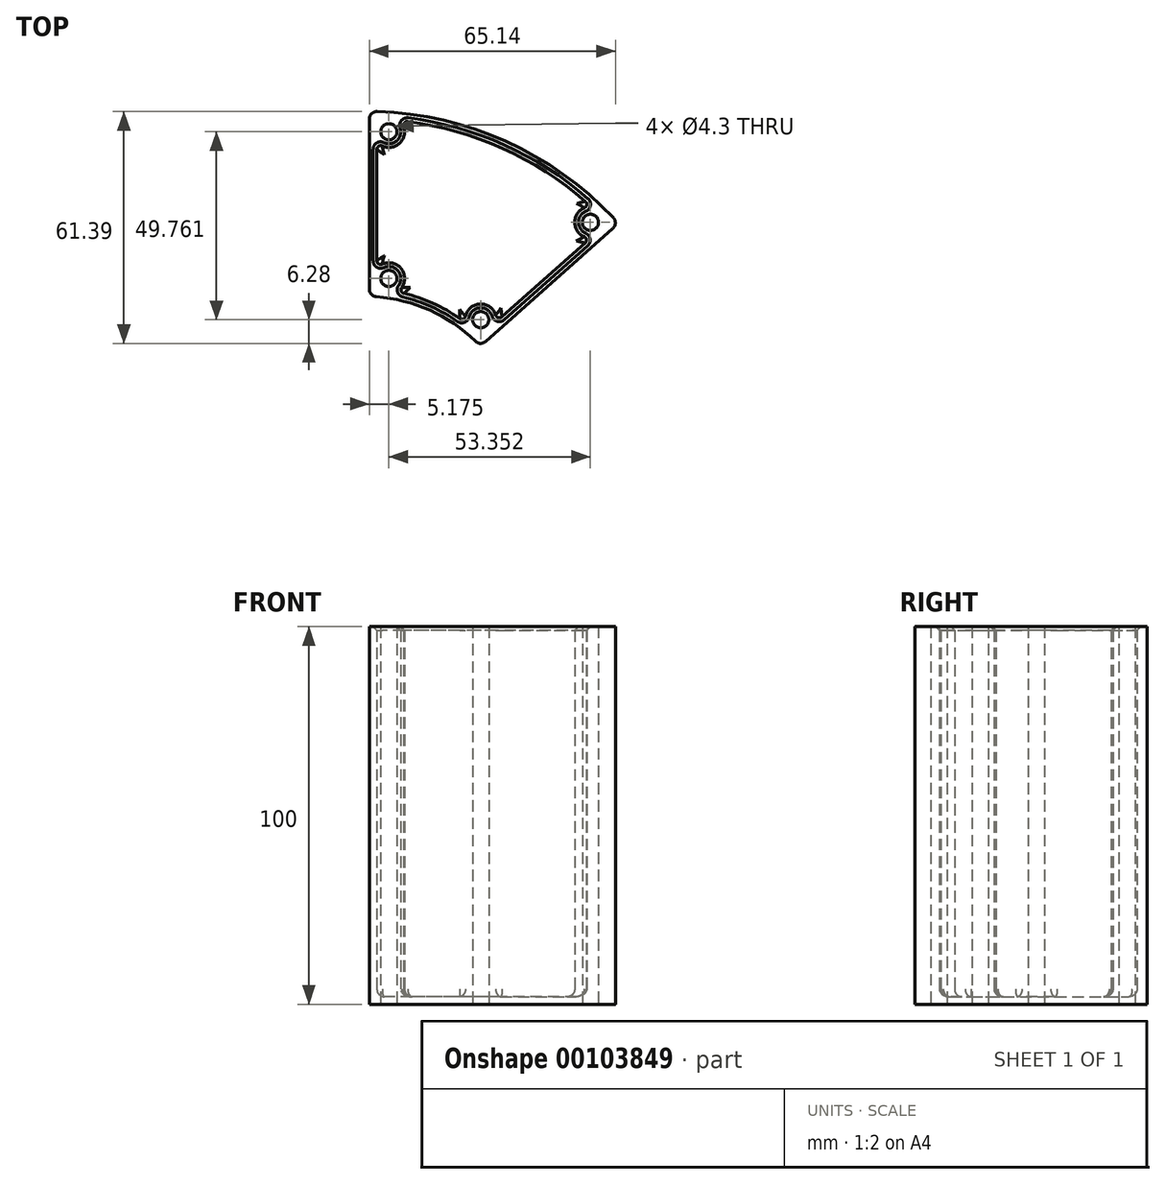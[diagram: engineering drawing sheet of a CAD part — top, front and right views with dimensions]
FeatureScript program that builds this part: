
annotation { "Feature Type Name" : "Feature", "Feature Type Description" : "" }
export const myFeature = defineFeature(function(context is Context, id is Id, definition is map)
    precondition{}
    {
        {
            var Q0;
            Q0=qCreatedBy(makeId("Top.planeOp"),FACE);
            var sketch = newSketch(context, id + "F0", { "sketchPlane" : qUnion([Q0])});
            skArc(sketch, "E0", {"start": v(30.28, 26.9) * mm, "mid": v(16.6, 36.94) * mm, "end": v(0, 40.5) * mm});
            skLineSegment(sketch, "E1", {"start": v(0, 40.5) * mm, "end": v(0, 91.5) * mm});
            skLineSegment(sketch, "E2", {"start": v(30.28, 26.9) * mm, "end": v(68.41, 60.76) * mm});
            skArc(sketch, "E3", {"start": v(0, 91.5) * mm, "mid": v(-37.5, -83.46) * mm, "end": v(68.41, 60.76) * mm});
            skArc(sketch, "E4", {"start": v(68.41, 60.76) * mm, "mid": v(37.5, 83.46) * mm, "end": v(0, 91.5) * mm});
            skLineSegment(sketch, "E5.0", {"start": v(1, 43.4) * mm, "end": v(1, 88.45) * mm});
            skArc(sketch, "E5.1", {"start": v(29.05, 29.63) * mm, "mid": v(17, 37.85) * mm, "end": v(2.86, 41.4) * mm});
            skLineSegment(sketch, "E5.2", {"start": v(31.78, 29.57) * mm, "end": v(65.47, 59.48) * mm});
            skArc(sketch, "E5.3", {"start": v(65.59, 62.36) * mm, "mid": v(37.1, 82.55) * mm, "end": v(3.07, 90.45) * mm});
            skCircle(sketch, "E6", {"center": v(6.17, 85.1) * mm, "radius": 2.15 * mm});
            skCircle(sketch, "E7", {"center": v(59.53, 61.13) * mm, "radius": 2.15 * mm});
            skCircle(sketch, "E8", {"center": v(30.5, 35.34) * mm, "radius": 2.15 * mm});
            skCircle(sketch, "E9", {"center": v(6.17, 46.26) * mm, "radius": 2.15 * mm});
            skLineSegment(sketch, "E10.0", {"start": v(3, 50.93) * mm, "end": v(3, 80.43) * mm});
            skArc(sketch, "E10.1", {"start": v(24.9, 35.67) * mm, "mid": v(17.83, 39.68) * mm, "end": v(10.14, 42.3) * mm});
            skLineSegment(sketch, "E10.2", {"start": v(36.09, 36.07) * mm, "end": v(58.15, 55.66) * mm});
            skArc(sketch, "E10.3", {"start": v(58.23, 66.65) * mm, "mid": v(36.27, 80.73) * mm, "end": v(11.16, 87.8) * mm});
            skArc(sketch, "E11", {"start": v(4.42, 81.34) * mm, "mid": v(8.96, 82.02) * mm, "end": v(10.1, 86.47) * mm});
            skArc(sketch, "E12", {"start": v(57.95, 64.97) * mm, "mid": v(55.38, 61.17) * mm, "end": v(57.88, 57.32) * mm});
            skArc(sketch, "E13", {"start": v(34.47, 36.53) * mm, "mid": v(30.36, 39.49) * mm, "end": v(26.45, 36.27) * mm});
            skArc(sketch, "E14", {"start": v(9.55, 43.86) * mm, "mid": v(9.37, 48.92) * mm, "end": v(4.42, 50.03) * mm});
            skPoint(sketch, "E15.visualSharp", {"position": v(9.12, 88.03) * mm});
            skArc(sketch, "E15.filletArc", {"start": v(11.16, 87.8) * mm, "mid": v(10.26, 87.43) * mm, "end": v(10.1, 86.47) * mm});
            skPoint(sketch, "E16.visualSharp", {"position": v(3, 82.43) * mm});
            skArc(sketch, "E16.filletArc", {"start": v(4.42, 81.34) * mm, "mid": v(3.46, 81.28) * mm, "end": v(3, 80.43) * mm});
            skPoint(sketch, "E17.visualSharp", {"position": v(3, 48.94) * mm});
            skArc(sketch, "E17.filletArc", {"start": v(3, 50.93) * mm, "mid": v(3.46, 50.09) * mm, "end": v(4.42, 50.03) * mm});
            skPoint(sketch, "E18.visualSharp", {"position": v(8.3, 42.7) * mm});
            skArc(sketch, "E18.filletArc", {"start": v(9.55, 43.86) * mm, "mid": v(9.43, 42.92) * mm, "end": v(10.14, 42.3) * mm});
            skPoint(sketch, "E19.visualSharp", {"position": v(26.41, 34.56) * mm});
            skArc(sketch, "E19.filletArc", {"start": v(24.9, 35.67) * mm, "mid": v(25.83, 35.56) * mm, "end": v(26.45, 36.27) * mm});
            skPoint(sketch, "E20.visualSharp", {"position": v(34.6, 34.74) * mm});
            skArc(sketch, "E20.filletArc", {"start": v(34.47, 36.53) * mm, "mid": v(35.15, 35.85) * mm, "end": v(36.09, 36.07) * mm});
            skPoint(sketch, "E21.visualSharp", {"position": v(59.64, 56.98) * mm});
            skArc(sketch, "E21.filletArc", {"start": v(58.15, 55.66) * mm, "mid": v(58.47, 56.56) * mm, "end": v(57.88, 57.32) * mm});
            skPoint(sketch, "E22.visualSharp", {"position": v(59.76, 65.27) * mm});
            skArc(sketch, "E22.filletArc", {"start": v(57.95, 64.97) * mm, "mid": v(58.56, 65.73) * mm, "end": v(58.23, 66.65) * mm});
            skPoint(sketch, "E23.visualSharp", {"position": v(1, 90.5) * mm});
            skArc(sketch, "E23.filletArc", {"start": v(3.07, 90.45) * mm, "mid": v(1.6, 89.89) * mm, "end": v(1, 88.45) * mm});
            skPoint(sketch, "E24.visualSharp", {"position": v(1, 41.49) * mm});
            skArc(sketch, "E24.filletArc", {"start": v(1, 43.4) * mm, "mid": v(1.54, 42.03) * mm, "end": v(2.86, 41.4) * mm});
            skPoint(sketch, "E25.visualSharp", {"position": v(30.36, 28.3) * mm});
            skArc(sketch, "E25.filletArc", {"start": v(29.05, 29.63) * mm, "mid": v(30.4, 29.06) * mm, "end": v(31.78, 29.57) * mm});
            skPoint(sketch, "E26.visualSharp", {"position": v(67, 60.84) * mm});
            skArc(sketch, "E26.filletArc", {"start": v(65.47, 59.48) * mm, "mid": v(66.14, 60.9) * mm, "end": v(65.59, 62.36) * mm});
            skSolve(sketch);
        }
        {
            var Q0;
            Q0=makeQuery(id+"F0.imprint","IMPRINT",FACE,{"disambiguationData":[TD([[makeQuery(id+"F0.imprint","IMPRINT",EDGE,{"derivedFrom":sQuery(id+"F0.wireOp",EDGE,"E5.0")}),-1.0]])]});
            var Q1;
            {var subQ1=sQuery(id+"F0.wireOp",EDGE,"b1673f46-570e-4e34-a5b0-88a3ac622ac5.0");Q1=makeQuery(id+"F0.imprint","IMPRINT",FACE,{"disambiguationData":[TD([[makeQuery(id+"F0.imprint","IMPRINT",EDGE,{"derivedFrom":subQ1}),1.0]])]});}
            var Q2;
            {var subQ1=sQuery(id+"F0.wireOp",EDGE,"b1673f46-570e-4e34-a5b0-88a3ac622ac5.0");Q2=makeQuery(id+"F0.imprint","IMPRINT",FACE,{"disambiguationData":[TD([[makeQuery(id+"F0.imprint","IMPRINT",EDGE,{"derivedFrom":subQ1}),-1.0]])]});}
            var Q3;
            Q3=makeQuery(id+"F0.imprint","IMPRINT",FACE,{"disambiguationData":[TD([[makeQuery(id+"F0.imprint","IMPRINT",EDGE,{"derivedFrom":sQuery(id+"F0.wireOp",EDGE,"E10.3")}),1.0]])]});
            var Q4;
            {var subQ1=sQuery(id+"F0.wireOp",EDGE,"b1673f46-570e-4e34-a5b0-88a3ac622ac5.2");Q4=makeQuery(id+"F0.imprint","IMPRINT",FACE,{"disambiguationData":[TD([[makeQuery(id+"F0.imprint","IMPRINT",EDGE,{"derivedFrom":subQ1}),-1.0]])]});}
            var Q5;
            {var subQ1=sQuery(id+"F0.wireOp",EDGE,"b1673f46-570e-4e34-a5b0-88a3ac622ac5.1");Q5=makeQuery(id+"F0.imprint","IMPRINT",FACE,{"disambiguationData":[TD([[makeQuery(id+"F0.imprint","IMPRINT",EDGE,{"derivedFrom":subQ1}),1.0]])]});}
            extrude(context, id + "F1", {"entities" : qUnion([Q0, Q1, Q2, Q3, Q4, Q5]), "depth" : 2 * mm});
        }
        {
            var Q0;
            Q0=makeQuery(id+"F0.imprint","IMPRINT",FACE,{"disambiguationData":[TD([[makeQuery(id+"F0.imprint","IMPRINT",EDGE,{"derivedFrom":sQuery(id+"F0.wireOp",EDGE,"E5.0")}),-1.0]])]});
            extrude(context, id + "F2", {"entities" : qUnion([Q0]), "depth" : 100 * mm});
        }
        {
            var Q0;
            Q0=makeQuery(id+"F2.opExtrude","SWEPT_BODY",BODY,{"disambiguationData":[OSD([sQuery(id+"F0.wireOp",EDGE,"E5.0"),sQuery(id+"F0.wireOp",EDGE,"E5.1"),sQuery(id+"F0.wireOp",EDGE,"E5.2"),sQuery(id+"F0.wireOp",EDGE,"E5.3"),sQuery(id+"F0.wireOp",EDGE,"E6"),sQuery(id+"F0.wireOp",EDGE,"E7"),sQuery(id+"F0.wireOp",EDGE,"E8"),sQuery(id+"F0.wireOp",EDGE,"E9"),sQuery(id+"F0.wireOp",EDGE,"E10.0"),sQuery(id+"F0.wireOp",EDGE,"E10.1"),sQuery(id+"F0.wireOp",EDGE,"E10.2"),sQuery(id+"F0.wireOp",EDGE,"E10.3"),sQuery(id+"F0.wireOp",EDGE,"E11"),sQuery(id+"F0.wireOp",EDGE,"E12"),sQuery(id+"F0.wireOp",EDGE,"E13"),sQuery(id+"F0.wireOp",EDGE,"E14"),sQuery(id+"F0.wireOp",EDGE,"E15.filletArc"),sQuery(id+"F0.wireOp",EDGE,"E16.filletArc"),sQuery(id+"F0.wireOp",EDGE,"E17.filletArc"),sQuery(id+"F0.wireOp",EDGE,"E18.filletArc"),sQuery(id+"F0.wireOp",EDGE,"E19.filletArc"),sQuery(id+"F0.wireOp",EDGE,"E20.filletArc"),sQuery(id+"F0.wireOp",EDGE,"E21.filletArc"),sQuery(id+"F0.wireOp",EDGE,"E22.filletArc"),sQuery(id+"F0.wireOp",EDGE,"E23.filletArc"),sQuery(id+"F0.wireOp",EDGE,"E24.filletArc"),sQuery(id+"F0.wireOp",EDGE,"E25.filletArc"),sQuery(id+"F0.wireOp",EDGE,"E26.filletArc")])]});
            var Q1;
            Q1=makeQuery(id+"F1.opExtrude","SWEPT_BODY",BODY,{"disambiguationData":[OSD([sQuery(id+"F0.wireOp",EDGE,"E5.0"),sQuery(id+"F0.wireOp",EDGE,"E5.1"),sQuery(id+"F0.wireOp",EDGE,"E5.2"),sQuery(id+"F0.wireOp",EDGE,"E5.3"),sQuery(id+"F0.wireOp",EDGE,"E6"),sQuery(id+"F0.wireOp",EDGE,"E7"),sQuery(id+"F0.wireOp",EDGE,"E8"),sQuery(id+"F0.wireOp",EDGE,"E9"),sQuery(id+"F0.wireOp",EDGE,"E23.filletArc"),sQuery(id+"F0.wireOp",EDGE,"E24.filletArc"),sQuery(id+"F0.wireOp",EDGE,"E25.filletArc"),sQuery(id+"F0.wireOp",EDGE,"E26.filletArc")])]});
            booleanBodies(context, id + "F3", {"operationType" : BooleanOperationType.UNION, "tools" : qUnion([Q0, Q1])});
        }
        {
            var Q0;
            Q0=makeQuery(id+"F3.opBoolean","INTERSECT",EDGE,{"derivedFrom":[makeQuery(id+"F1.opExtrude","CAP_FACE",FACE,{"disambiguationData":[OSD([sQuery(id+"F0.wireOp",EDGE,"E5.0"),sQuery(id+"F0.wireOp",EDGE,"E5.1"),sQuery(id+"F0.wireOp",EDGE,"E5.2"),sQuery(id+"F0.wireOp",EDGE,"E5.3"),sQuery(id+"F0.wireOp",EDGE,"E6"),sQuery(id+"F0.wireOp",EDGE,"E7"),sQuery(id+"F0.wireOp",EDGE,"E8"),sQuery(id+"F0.wireOp",EDGE,"E9"),sQuery(id+"F0.wireOp",EDGE,"E23.filletArc"),sQuery(id+"F0.wireOp",EDGE,"E24.filletArc"),sQuery(id+"F0.wireOp",EDGE,"E25.filletArc"),sQuery(id+"F0.wireOp",EDGE,"E26.filletArc")])],"isStart":false}),makeQuery(id+"F2.opExtrude","SWEPT_FACE",FACE,{"disambiguationData":[OSD([sQuery(id+"F0.wireOp",EDGE,"E10.0")])]})]});
            var Q1;
            Q1=makeQuery(id+"F3.opBoolean","INTERSECT",EDGE,{"derivedFrom":[makeQuery(id+"F1.opExtrude","CAP_FACE",FACE,{"disambiguationData":[OSD([sQuery(id+"F0.wireOp",EDGE,"E5.0"),sQuery(id+"F0.wireOp",EDGE,"E5.1"),sQuery(id+"F0.wireOp",EDGE,"E5.2"),sQuery(id+"F0.wireOp",EDGE,"E5.3"),sQuery(id+"F0.wireOp",EDGE,"E6"),sQuery(id+"F0.wireOp",EDGE,"E7"),sQuery(id+"F0.wireOp",EDGE,"E8"),sQuery(id+"F0.wireOp",EDGE,"E9"),sQuery(id+"F0.wireOp",EDGE,"E23.filletArc"),sQuery(id+"F0.wireOp",EDGE,"E24.filletArc"),sQuery(id+"F0.wireOp",EDGE,"E25.filletArc"),sQuery(id+"F0.wireOp",EDGE,"E26.filletArc")])],"isStart":false}),makeQuery(id+"F2.opExtrude","SWEPT_FACE",FACE,{"disambiguationData":[OSD([sQuery(id+"F0.wireOp",EDGE,"E16.filletArc")])]})]});
            fillet(context, id + "F4", {"entities" : qUnion([Q0, Q1]), "radius" : 2 * mm, "tangentPropagation" : true, "allowEdgeOverflow" : false});
        }
        {
            var Q0;
            Q0=makeQuery(id+"F2.opExtrude","CAP_EDGE",EDGE,{"disambiguationData":[OSD([sQuery(id+"F0.wireOp",EDGE,"E10.0")])],"isStart":false});
            var Q1;
            Q1=makeQuery(id+"F2.opExtrude","CAP_EDGE",EDGE,{"disambiguationData":[OSD([sQuery(id+"F0.wireOp",EDGE,"E17.filletArc")])],"isStart":false});
            var Q2;
            Q2=makeQuery(id+"F2.opExtrude","CAP_EDGE",EDGE,{"disambiguationData":[OSD([sQuery(id+"F0.wireOp",EDGE,"E14")])],"isStart":false});
            var Q3;
            Q3=makeQuery(id+"F2.opExtrude","CAP_EDGE",EDGE,{"disambiguationData":[OSD([sQuery(id+"F0.wireOp",EDGE,"E18.filletArc")])],"isStart":false});
            var Q4;
            Q4=makeQuery(id+"F2.opExtrude","CAP_EDGE",EDGE,{"disambiguationData":[OSD([sQuery(id+"F0.wireOp",EDGE,"E10.1")])],"isStart":false});
            var Q5;
            Q5=makeQuery(id+"F2.opExtrude","CAP_EDGE",EDGE,{"disambiguationData":[OSD([sQuery(id+"F0.wireOp",EDGE,"E19.filletArc")])],"isStart":false});
            var Q6;
            Q6=makeQuery(id+"F2.opExtrude","CAP_EDGE",EDGE,{"disambiguationData":[OSD([sQuery(id+"F0.wireOp",EDGE,"E13")])],"isStart":false});
            var Q7;
            Q7=makeQuery(id+"F2.opExtrude","CAP_EDGE",EDGE,{"disambiguationData":[OSD([sQuery(id+"F0.wireOp",EDGE,"E20.filletArc")])],"isStart":false});
            var Q8;
            Q8=makeQuery(id+"F2.opExtrude","CAP_EDGE",EDGE,{"disambiguationData":[OSD([sQuery(id+"F0.wireOp",EDGE,"E10.2")])],"isStart":false});
            var Q9;
            Q9=makeQuery(id+"F2.opExtrude","CAP_EDGE",EDGE,{"disambiguationData":[OSD([sQuery(id+"F0.wireOp",EDGE,"E21.filletArc")])],"isStart":false});
            var Q10;
            Q10=makeQuery(id+"F2.opExtrude","CAP_EDGE",EDGE,{"disambiguationData":[OSD([sQuery(id+"F0.wireOp",EDGE,"E12")])],"isStart":false});
            var Q11;
            Q11=makeQuery(id+"F2.opExtrude","CAP_EDGE",EDGE,{"disambiguationData":[OSD([sQuery(id+"F0.wireOp",EDGE,"E22.filletArc")])],"isStart":false});
            var Q12;
            Q12=makeQuery(id+"F2.opExtrude","CAP_EDGE",EDGE,{"disambiguationData":[OSD([sQuery(id+"F0.wireOp",EDGE,"E10.3")])],"isStart":false});
            var Q13;
            Q13=makeQuery(id+"F2.opExtrude","CAP_EDGE",EDGE,{"disambiguationData":[OSD([sQuery(id+"F0.wireOp",EDGE,"E11")])],"isStart":false});
            var Q14;
            Q14=makeQuery(id+"F2.opExtrude","CAP_EDGE",EDGE,{"disambiguationData":[OSD([sQuery(id+"F0.wireOp",EDGE,"E15.filletArc")])],"isStart":false});
            var Q15;
            Q15=makeQuery(id+"F2.opExtrude","CAP_EDGE",EDGE,{"disambiguationData":[OSD([sQuery(id+"F0.wireOp",EDGE,"E16.filletArc")])],"isStart":false});
            chamfer(context, id + "F5", {"entities" : qUnion([Q0, Q1, Q2, Q3, Q4, Q5, Q6, Q7, Q8, Q9, Q10, Q11, Q12, Q13, Q14, Q15]), "width" : 1 * mm, "tangentPropagation" : true});
        }
    });
